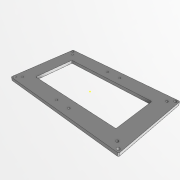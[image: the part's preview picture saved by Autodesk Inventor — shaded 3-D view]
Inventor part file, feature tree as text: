
AUTODESK INVENTOR PART (.ipt)
format: ipt  version: 2018 (Build 220112000, 112)  size: 189,440 bytes
history: native  units: in
note: dims shown in document units (in); Inventor stores cm internally (conversion verified against a paired STEP export)
features: sketch x4, extrude x3, hole x1, fillet x1
ambient origin geometry x8: Origin, YZ Plane, XZ Plane, XY Plane, X Axis, Y Axis, Z Axis, Center Point
bodies: Solid1 (feature_tree)
feature tree (9):
  sketch  "Sketch1"  dims[d0=9.4488in d2=1.1811in]
  extrude  "Extrusion1"  Depth=1.1811in
  extrude  "Extrusion2"  Depth=0.25in TaperAngle=0.0deg
  extrude  "Extrusion3"  Depth=3.937in
  hole  "Hole1"  [1 undecoded]
  fillet  "Fillet1"  Radius=3.937in
  sketch  "Sketch5"  dims[d9=0.3937in d10=0.3937in d11=3.937in d12=4.8425in d13=0.7874in d14=0.1654in d15=0.1575in d16=0.1575in d17=0.1654in d18=0.1575in d19=0.1575in d20=0.1654in d21=0.1575in d22=0.1575in d23=0.1654in d24=0.1575in d25=0.1575in d26=0.1654in d27=0.1575in d28=0.1575in d29=0.1654in d30=0.1575in d31=0.1575in d32=0.1654in d33=0.1575in d34=0.1575in d35=0.1654in d36=0.1575in d37=0.1575in d38=0.3937in d39=0.25in d40=0.0in d41=0.1969in d42=0.1969in d43=0.1969in d44=0.1969in d45=0.1969in d46=0.1969in d47=0.1969in d48=0.1969in d49=0.1969in d50=0.1969in d51=0.1969in d52=0.1969in d53=0.25in d54=0.0in d55=1.1811in d56=0.1969in d57=0.1969in d58=0.2008in d59=0.2362in d60=0.1575in d61=0.0787in d62=90.0deg d63=0.315in d64=0.8108in d65=0.0787in]
  sketch  "Sketch2"  dims[d4=5.6299in d5=0.25in d6=0.0in]
  sketch  "Sketch3"  dims[d7=4.8425in d8=3.937in]
note: 1 required parameter value undecoded (feature->parameter linkage not recoverable at this tier; creation-order binding heuristic only, values carry confidence <= 0.55)
